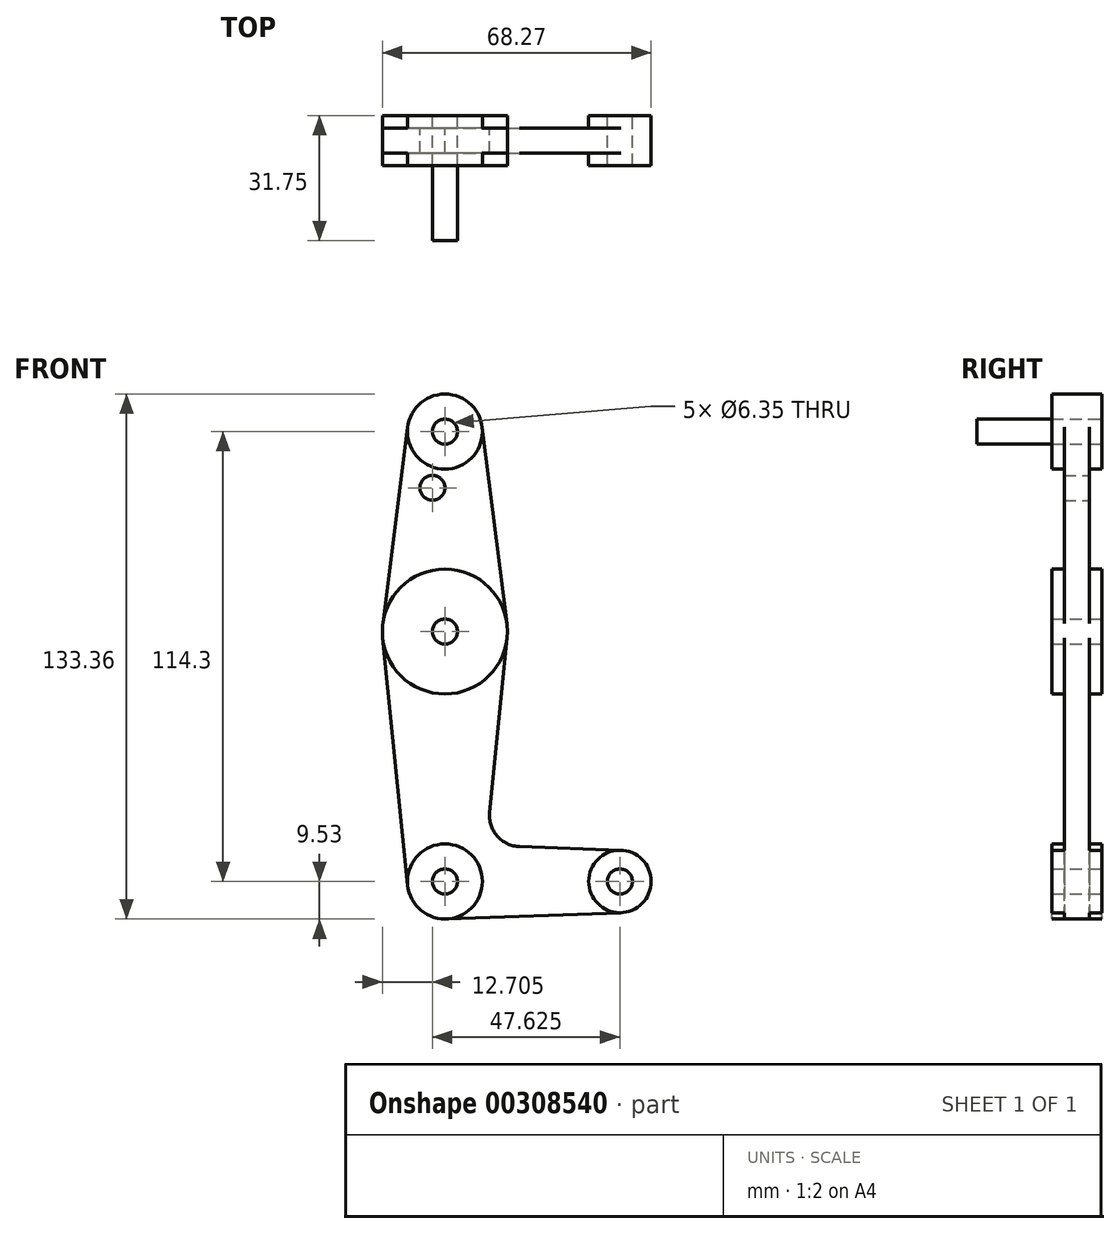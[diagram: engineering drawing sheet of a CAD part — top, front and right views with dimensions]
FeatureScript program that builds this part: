
annotation { "Feature Type Name" : "Feature", "Feature Type Description" : "" }
export const myFeature = defineFeature(function(context is Context, id is Id, definition is map)
    precondition{}
    {
        {
            var Q0;
            Q0=qCreatedBy(makeId("Front.planeOp"),FACE);
            var sketch = newSketch(context, id + "F0", { "sketchPlane" : qUnion([Q0])});
            skCircle(sketch, "E0", {"center": v(0, 0) * mm, "radius": 3.18 * mm});
            skCircle(sketch, "E1", {"center": v(0, 0) * mm, "radius": 9.53 * mm});
            skCircle(sketch, "E2", {"center": v(44.45, 0) * mm, "radius": 3.18 * mm});
            skCircle(sketch, "E3", {"center": v(44.45, 0) * mm, "radius": 7.94 * mm});
            skCircle(sketch, "E4", {"center": v(0, 63.5) * mm, "radius": 3.18 * mm});
            skCircle(sketch, "E5", {"center": v(0, 63.5) * mm, "radius": 15.88 * mm});
            skCircle(sketch, "E6", {"center": v(0, 114.3) * mm, "radius": 3.18 * mm});
            skCircle(sketch, "E7", {"center": v(0, 114.3) * mm, "radius": 9.53 * mm});
            skCircle(sketch, "E8", {"center": v(-3.17, 100.03) * mm, "radius": 3.18 * mm});
            skLineSegment(sketch, "E9", {"start": v(-9.45, 115.5) * mm, "end": v(-15.75, 65.48) * mm});
            skLineSegment(sketch, "E10", {"start": v(9.45, 115.5) * mm, "end": v(15.75, 65.48) * mm});
            skLineSegment(sketch, "E11", {"start": v(15.8, 61.91) * mm, "end": v(11.34, 17.6) * mm});
            skLineSegment(sketch, "E12", {"start": v(-15.8, 61.91) * mm, "end": v(-9.48, -0.95) * mm});
            skLineSegment(sketch, "E13", {"start": v(18.97, 8.85) * mm, "end": v(44.73, 7.93) * mm});
            skLineSegment(sketch, "E14", {"start": v(0.34, -9.52) * mm, "end": v(44.73, -7.93) * mm});
            skArc(sketch, "E15.filletArc", {"start": v(11.34, 17.6) * mm, "mid": v(13.26, 11.57) * mm, "end": v(18.97, 8.85) * mm});
            skSolve(sketch);
        }
        {
            var Q0;
            Q0=qSketchRegion(id+"F0",true);
            extrude(context, id + "F1", {"entities" : qUnion([Q0]), "endBound" : BoundingType.SYMMETRIC, "depth" : 6.35 * mm});
        }
        {
            var Q0;
            Q0=makeQuery(id+"F0.imprint","IMPRINT",FACE,{"disambiguationData":[TD([[makeQuery(id+"F0.imprint","IMPRINT",EDGE,{"derivedFrom":sQuery(id+"F0.wireOp",EDGE,"E0")}),-1.0]])]});
            var Q1;
            Q1=makeQuery(id+"F0.imprint","IMPRINT",FACE,{"disambiguationData":[TD([[makeQuery(id+"F0.imprint","IMPRINT",EDGE,{"derivedFrom":sQuery(id+"F0.wireOp",EDGE,"E4")}),-1.0]])]});
            var Q2;
            Q2=makeQuery(id+"F0.imprint","IMPRINT",FACE,{"disambiguationData":[TD([[makeQuery(id+"F0.imprint","IMPRINT",EDGE,{"derivedFrom":sQuery(id+"F0.wireOp",EDGE,"E6")}),-1.0]])]});
            var Q3;
            Q3=makeQuery(id+"F0.imprint","IMPRINT",FACE,{"disambiguationData":[TD([[makeQuery(id+"F0.imprint","IMPRINT",EDGE,{"derivedFrom":sQuery(id+"F0.wireOp",EDGE,"E2")}),-1.0]])]});
            extrude(context, id + "F2", {"entities" : qUnion([Q0, Q1, Q2, Q3]), "operationType" : NewBodyOperationType.ADD, "endBound" : BoundingType.SYMMETRIC, "depth" : 12.7 * mm});
        }
        {
            var Q0;
            Q0=makeQuery(id+"F0.imprint","IMPRINT",FACE,{"disambiguationData":[TD([[makeQuery(id+"F0.imprint","IMPRINT",EDGE,{"derivedFrom":sQuery(id+"F0.wireOp",EDGE,"E6")}),1.0]])]});
            var Q1;
            Q1=makeQuery(id+"F2.opExtrude","CAP_FACE",FACE,{"disambiguationData":[OSD([sQuery(id+"F0.wireOp",EDGE,"E6"),sQuery(id+"F0.wireOp",EDGE,"E7")])],"isStart":true});
            extrude(context, id + "F3", {"entities" : qUnion([Q0]), "depth" : 25.4 * mm, "hasSecondDirection" : true, "secondDirectionBound" : SecondDirectionBoundingType.UP_TO_SURFACE, "secondDirectionOppositeDirection" : true, "secondDirectionBoundEntityFace" : qUnion([Q1]), "secondDirectionDepth" : 25.4 * mm});
        }
    });
